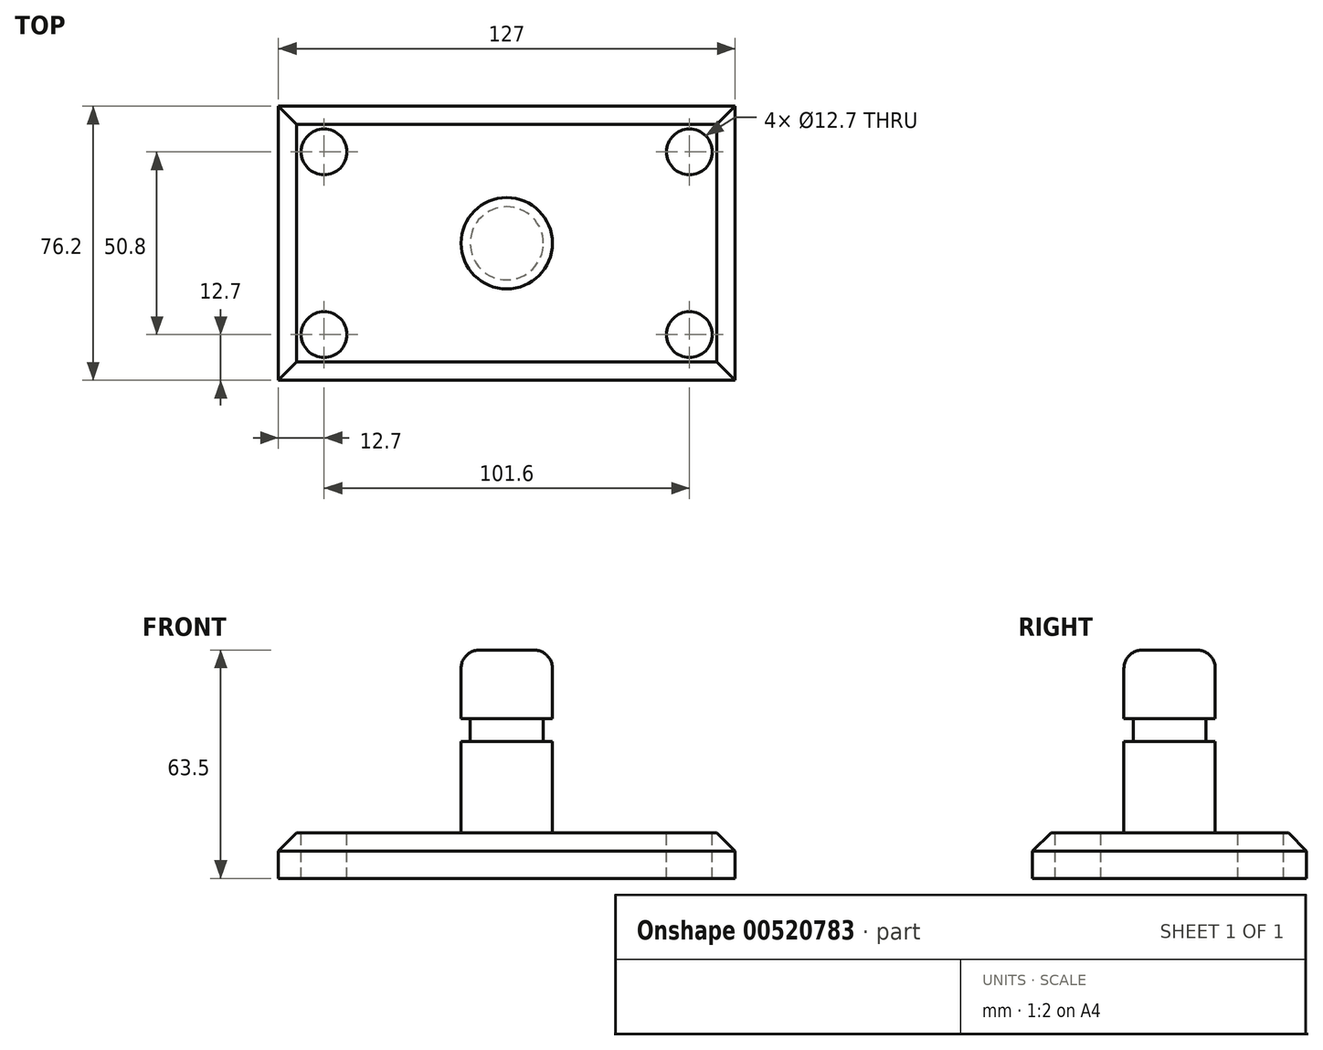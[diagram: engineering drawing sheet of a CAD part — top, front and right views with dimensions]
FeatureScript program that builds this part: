
annotation { "Feature Type Name" : "Feature", "Feature Type Description" : "" }
export const myFeature = defineFeature(function(context is Context, id is Id, definition is map)
    precondition{}
    {
        {
            var Q0;
            Q0=qCreatedBy(makeId("Top.planeOp"),FACE);
            var sketch = newSketch(context, id + "F0", { "sketchPlane" : qUnion([Q0])});
            skLineSegment(sketch, "E0.bottom", {"start": v(63.5, 38.1) * mm, "end": v(-63.5, 38.1) * mm});
            skLineSegment(sketch, "E0.top", {"start": v(63.5, -38.1) * mm, "end": v(-63.5, -38.1) * mm});
            skLineSegment(sketch, "E0.left", {"start": v(63.5, 38.1) * mm, "end": v(63.5, -38.1) * mm});
            skLineSegment(sketch, "E0.right", {"start": v(-63.5, 38.1) * mm, "end": v(-63.5, -38.1) * mm});
            skPoint(sketch, "E0.middle", {"position": v(0, 0) * mm});
            skSolve(sketch);
        }
        {
            var Q0;
            Q0=makeQuery(id+"F0.imprint","IMPRINT",FACE,{"disambiguationData":[TD([[makeQuery(id+"F0.imprint","IMPRINT",EDGE,{"derivedFrom":sQuery(id+"F0.wireOp",EDGE,"E0.bottom")}),1.0]])]});
            extrude(context, id + "F1", {"entities" : qUnion([Q0]), "depth" : 12.7 * mm, "offsetDistance" : 25.4 * mm});
        }
        {
            var Q0;
            Q0=makeQuery(id+"F1.opExtrude","CAP_FACE",FACE,{"disambiguationData":[OSD([sQuery(id+"F0.wireOp",EDGE,"E0.bottom"),sQuery(id+"F0.wireOp",EDGE,"E0.top"),sQuery(id+"F0.wireOp",EDGE,"E0.left"),sQuery(id+"F0.wireOp",EDGE,"E0.right")])],"isStart":false});
            var sketch = newSketch(context, id + "F2", { "sketchPlane" : qUnion([Q0])});
            skCircle(sketch, "E1", {"center": v(-50.8, 25.4) * mm, "radius": 6.35 * mm});
            skCircle(sketch, "E2", {"center": v(50.8, 25.4) * mm, "radius": 6.35 * mm});
            skCircle(sketch, "E3", {"center": v(-50.8, -25.4) * mm, "radius": 6.35 * mm});
            skCircle(sketch, "E4", {"center": v(50.8, -25.4) * mm, "radius": 6.35 * mm});
            skSolve(sketch);
        }
        {
            var Q0;
            Q0 = qSketchRegion(id + "F2", true);
            extrude(context, id + "F3", {"entities" : qUnion([Q0]), "operationType" : NewBodyOperationType.REMOVE, "endBound" : BoundingType.THROUGH_ALL, "oppositeDirection" : true, "depth" : 25.4 * mm, "offsetDistance" : 25.4 * mm});
        }
        {
            var Q0;
            Q0=qCreatedBy(makeId("Right.planeOp"),FACE);
            var sketch = newSketch(context, id + "F4", { "sketchPlane" : qUnion([Q0])});
            skLineSegment(sketch, "E5.bottom", {"start": v(0, 12.7) * mm, "end": v(12.7, 12.7) * mm});
            skLineSegment(sketch, "E5.top", {"start": v(0, 63.5) * mm, "end": v(12.7, 63.5) * mm});
            skLineSegment(sketch, "E5.left", {"start": v(0, 12.7) * mm, "end": v(0, 63.5) * mm});
            skLineSegment(sketch, "E5.right", {"start": v(12.7, 12.7) * mm, "end": v(12.7, 63.5) * mm});
            skSolve(sketch);
        }
        {
            var Q0;
            Q0=makeQuery(id+"F4.imprint","IMPRINT",FACE,{"disambiguationData":[TD([[makeQuery(id+"F4.imprint","IMPRINT",EDGE,{"derivedFrom":sQuery(id+"F4.wireOp",EDGE,"E5.bottom")}),1.0]])]});
            var Q1;
            Q1=sQuery(id+"F4.wireOp",EDGE,"E5.left");
            revolve(context, id + "F5", {"operationType" : NewBodyOperationType.ADD, "entities" : qUnion([Q0]), "axis" : qUnion([Q1]), "revolveType" : RevolveType.FULL});
        }
        {
            var Q0;
            Q0=qCreatedBy(makeId("Front.planeOp"),FACE);
            var sketch = newSketch(context, id + "F6", { "sketchPlane" : qUnion([Q0])});
            skLineSegment(sketch, "E6.bottom", {"start": v(10.16, 44.45) * mm, "end": v(20.02, 44.45) * mm});
            skLineSegment(sketch, "E6.top", {"start": v(10.16, 38.1) * mm, "end": v(20.02, 38.1) * mm});
            skLineSegment(sketch, "E6.left", {"start": v(10.16, 44.45) * mm, "end": v(10.16, 38.1) * mm});
            skLineSegment(sketch, "E6.right", {"start": v(20.02, 44.45) * mm, "end": v(20.02, 38.1) * mm});
            skSolve(sketch);
        }
        {
            var Q0;
            Q0=makeQuery(id+"F6.imprint","IMPRINT",FACE,{"disambiguationData":[TD([[makeQuery(id+"F6.imprint","IMPRINT",EDGE,{"derivedFrom":sQuery(id+"F6.wireOp",EDGE,"E6.bottom")}),-1.0]])]});
            var Q1;
            Q1=makeQuery(id+"F5.opRevolve","SWEPT_FACE",FACE,{"disambiguationData":[OSD([sQuery(id+"F4.wireOp",EDGE,"E5.right")])]});
            revolve(context, id + "F7", {"operationType" : NewBodyOperationType.REMOVE, "entities" : qUnion([Q0]), "axis" : qUnion([Q1]), "revolveType" : RevolveType.FULL, "oppositeDirection" : true});
        }
        {
            var Q0;
            Q0=makeQuery(id+"F5.opRevolve","SWEPT_EDGE",EDGE,{"disambiguationData":[OSD([sQuery(id+"F4.wireOp",EDGE,"E5.bottom"),sQuery(id+"F4.wireOp",EDGE,"E5.right")])]});
            var Q1;
            Q1=makeQuery(id+"F5.opRevolve","SWEPT_EDGE",EDGE,{"disambiguationData":[OSD([sQuery(id+"F4.wireOp",EDGE,"E5.top"),sQuery(id+"F4.wireOp",EDGE,"E5.right")])]});
            fillet(context, id + "F8", {"entities" : qUnion([Q0, Q1]), "radius" : 5.08 * mm, "tangentPropagation" : true, "allowEdgeOverflow" : false});
        }
        {
            var Q0;
            Q0=makeQuery(id+"F1.opExtrude","CAP_EDGE",EDGE,{"disambiguationData":[OSD([sQuery(id+"F0.wireOp",EDGE,"E0.right")])],"isStart":false});
            var Q1;
            Q1=makeQuery(id+"F1.opExtrude","CAP_EDGE",EDGE,{"disambiguationData":[OSD([sQuery(id+"F0.wireOp",EDGE,"E0.top")])],"isStart":false});
            var Q2;
            Q2=makeQuery(id+"F1.opExtrude","CAP_EDGE",EDGE,{"disambiguationData":[OSD([sQuery(id+"F0.wireOp",EDGE,"E0.left")])],"isStart":false});
            var Q3;
            Q3=makeQuery(id+"F1.opExtrude","CAP_EDGE",EDGE,{"disambiguationData":[OSD([sQuery(id+"F0.wireOp",EDGE,"E0.bottom")])],"isStart":false});
            chamfer(context, id + "F9", {"entities" : qUnion([Q0, Q1, Q2, Q3]), "width" : 5.08 * mm, "tangentPropagation" : true});
        }
    });
